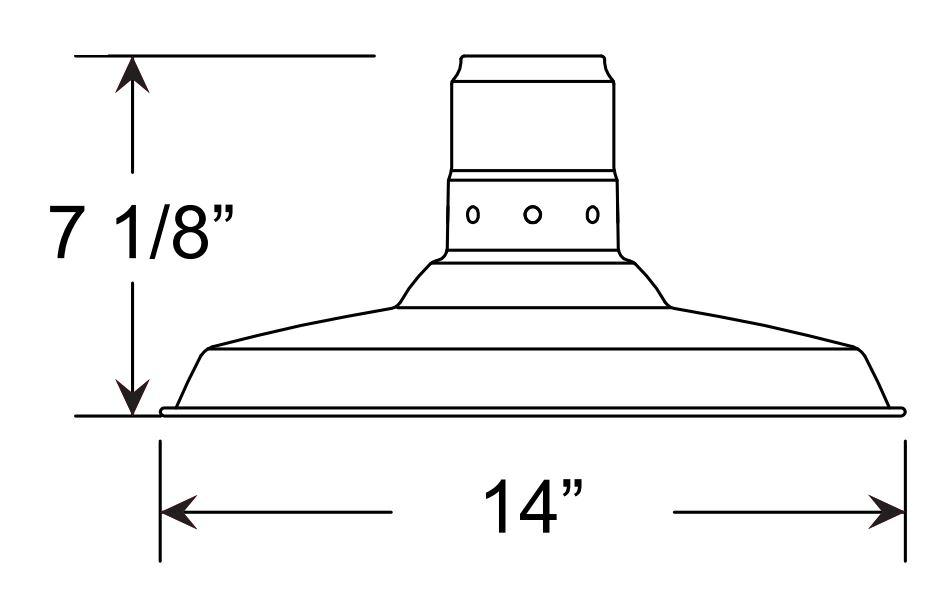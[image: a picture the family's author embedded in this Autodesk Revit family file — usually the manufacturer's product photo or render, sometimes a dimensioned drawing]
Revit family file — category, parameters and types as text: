
# Revit family: Mini Bella Vista_Flare_MB
name_source: partatom
category: Lighting Fixtures
units: mm (PartAtom-declared; Revit-internal decimal feet)

## family parameters
Always vertical = Yes
Cut with Voids When Loaded = No
Light Source = Yes
OmniClass Number = 23.80.70.00
OmniClass Title = Lighting
Part Type = Normal
Room Calculation Point = No
Round Connector Dimension = Use Diameter
Shared = No
Work Plane-Based = No

## types (3) — shared parameters
Body Colour = Spun aluminium
Body Material = body
Bulb = BULB
Color Filter = 16777215
Construction Material = Heavy Duty spun aluminum.
Default Elevation = 0' - 0"
Description = 120-277 Voltage
Dimming = 1%
Dimming Lamp Color Temperature Shift = <None>
GLASS = Glass
Inside body material = INSIDE BODY MATERIAL
Load Classification = Lighting
Manufacturer = ANP Lighting
Power Factor = 1
Tilt Angle = 90.00°
URL = https://www.anplighting.com
Voltage = 277 V
Warranty = 5 year limited warranty

## per-type parameters (varying)
| type | Apparent Load | CRI | Efficiency | Fixture Diameter | Fixture Height | Lamp | Life | MBVF12 | MBVF14 | MBVF16 | Photometric Web File | Wattage Comments | Weight |
| MBVF12 | 100 VA | >90 | 65-125 lumens per watt | 1' - 0" | 0' - 11" | 100W MAX MEDIUM BASE | L70 50,000 hours | Yes | No | No | MBVF12M016LDDW40K-IES.ies | 100W | 0.80 lb |
| MBVF14 | 200 VA | >90 | 65-125 lumens per watt | 1' - 2" | 0' - 11 1/2" | 200W MAX MEDIUM BASE | L70 50,000 hours | No | Yes | No | MBVF14M024LDDW40K.ies | 200W | 0.95 lb |
| MBVF16 | 200 VA | >70 | 80-116 lumens per watt | 1' - 4" | 1' - 0" | 200W MAX MEDIUM BASE | L70 60,000 hours | No | No | Yes | MBVF16E050LDST540K.ies | 200W | 1.25 lb |

note: column(s) folded — value = type name in every type: Model

## geometry (parser evidence)
native form markers: Sweep x29
no freeform markers — native parametric forms only
